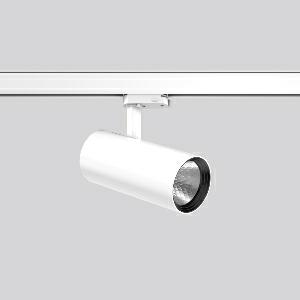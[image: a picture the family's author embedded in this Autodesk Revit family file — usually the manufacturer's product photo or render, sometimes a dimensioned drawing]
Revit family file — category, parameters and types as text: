
# Revit family: deecos_s_mini_742203_002_76_526d
name_source: partatom
category: Lighting Fixtures
units: mm (PartAtom-declared; Revit-internal decimal feet)

## family parameters
Cut with Voids When Loaded = No
Host = Face
Light Source = No
Part Type = Normal
Room Calculation Point = No
Round Connector Dimension = Use Diameter
Shared = No

## types (1)
- DEECOS S mini (1 x LED Modul 930, 3550 lm, 3000)
    Apparent Load = 29 VA
    Approval mark = CE
    CIE Flux Codes = 100 100 100 100 100
    Color Rendering = 90
    Color Temperature = 3000
    Default Elevation = 1800 mm
    Description = Series: DEECOS S mini
LED surface-mounted projector in modern design with no visible cooling ribs. Housing: die-cast aluminium, powder-coated. Rotation range: 356°. Swivel range: 90°. Black plastic ring and recessed LED to prevent glare from the side. Optical assembly with reflector made of MIRO-Silver with 98% total light reflection for outstanding efficiency - can be changed without tools. Best colour rendering index Ra>90. With adapter for RZB 3-circuit DALI tracks. Suitable for Track on ceiling, Wall track. High quality converter without flickering and stroboscopic effect. The following accessories can be mounted without use of tools: interchangeable lenses, decorative glasses, honeycomb louvre, clear and frosted diffusers, white interchangeable plastic ring. 
Colour: traffic white, matt (RAL 9016)
Diameter: 87 mm
Height: 214 mm
Lamp: LED
Socket: without socket
Colour temperature: 3000K
Colour rendering index (CRI): 92
System power: 29 W
Rated luminous flux: 3550 lm
Luminous efficiency: 122 lm/W
Control gear: Converter, dimmable, DALI
Protection class: I
Type of protection: IP 20
    Height = 214 mm
    Lamp = 1 x LED Modul 930
    Lamp Light Flux = 3550 lm
    Lamp count = 1
    Length = 87 mm
    Lifetime = 50000 h
    Luminous efficacy = 122 lm/W
    Manufacturer = RZB
    ModVariant = No
    Model = 742203.002.76
    Mounting Place = Ceiling
    Mounting Type = Rail mounted
    Number of Poles = 1
    OnlyDefault = Yes
    Power Factor = 1
    Product Name = DEECOS S mini
    Product group = Track mounted projectors
    ProductGroupID = 301
    Protection Class = Protection class I
    Protection Degree = IP 20
    RLX_Detail_Level = 1
    RLX_Emergency_Light_Flux = 0 lm
    RLX_Emergency_Type = 0
    RLX_Emergency_Type_DB = No
    RlxData = <blob elided: 35001 chars, md5=ea1fdf59>
    Socket = socket
    Standby Power = 0 W
    System Light Flux = 3550 lm
    System Power = 29 W
    Type Comments = Product without accessories
    Type Image = 741926.002.jpg
    URL = http://relux.com
    VarID = ---
    Voltage = 230 V
    Voltage Range = 220-240 V
    Weight = 0.00 kg
    Width = 0 mm  [stored 0 ft]

note: [stored X ft] marks values corroborated as IEEE doubles in the binary element streams (Revit-internal decimal feet)

## geometry (parser evidence)
native form markers: Blend x4, Sweep x12
no freeform markers — native parametric forms only
